# Revit family: C_SWC10x120_2DO_CAD_MULT_Prod
name_source: partatom
category: Detail Items
revit_build: Autodesk Revit 2015 (Build: 20140606_1530(x64)
units: mm (PartAtom-declared; Revit-internal decimal feet)

## types (2) — shared parameters
Density = 0.04 kg
Description = Screws
EPD = https://www.strongtie.eu
ETA / DoP = https://www.strongtie.eu
Manufacturer = Simpson Strong-Tie
Model = SWC10x120
Model Disclaimer = Contact Simpson Strong-Tie Company  for more information
Model ID = 0118194840527559738407544133118116293011
Name = SWC10x120
ObjectType = SWC10x120
Product Material = ElectroGalvanised
Product Type = Screws
Reference = 76917
Technical datasheet = https://www.strongtie.eu
URL = www.strongtie.eu
UniClass Number = Pr_20_29_76_98
UniClass Title = Wood screws

## per-type parameters (varying)
| type | _visiblefront | _visibletop |
| SST_SWC10x120_Front | Yes | No |
| SST_SWC10x120_Top | No | Yes |

## geometry (parser evidence)
native form markers: Blend x4
no freeform markers — native parametric forms only
